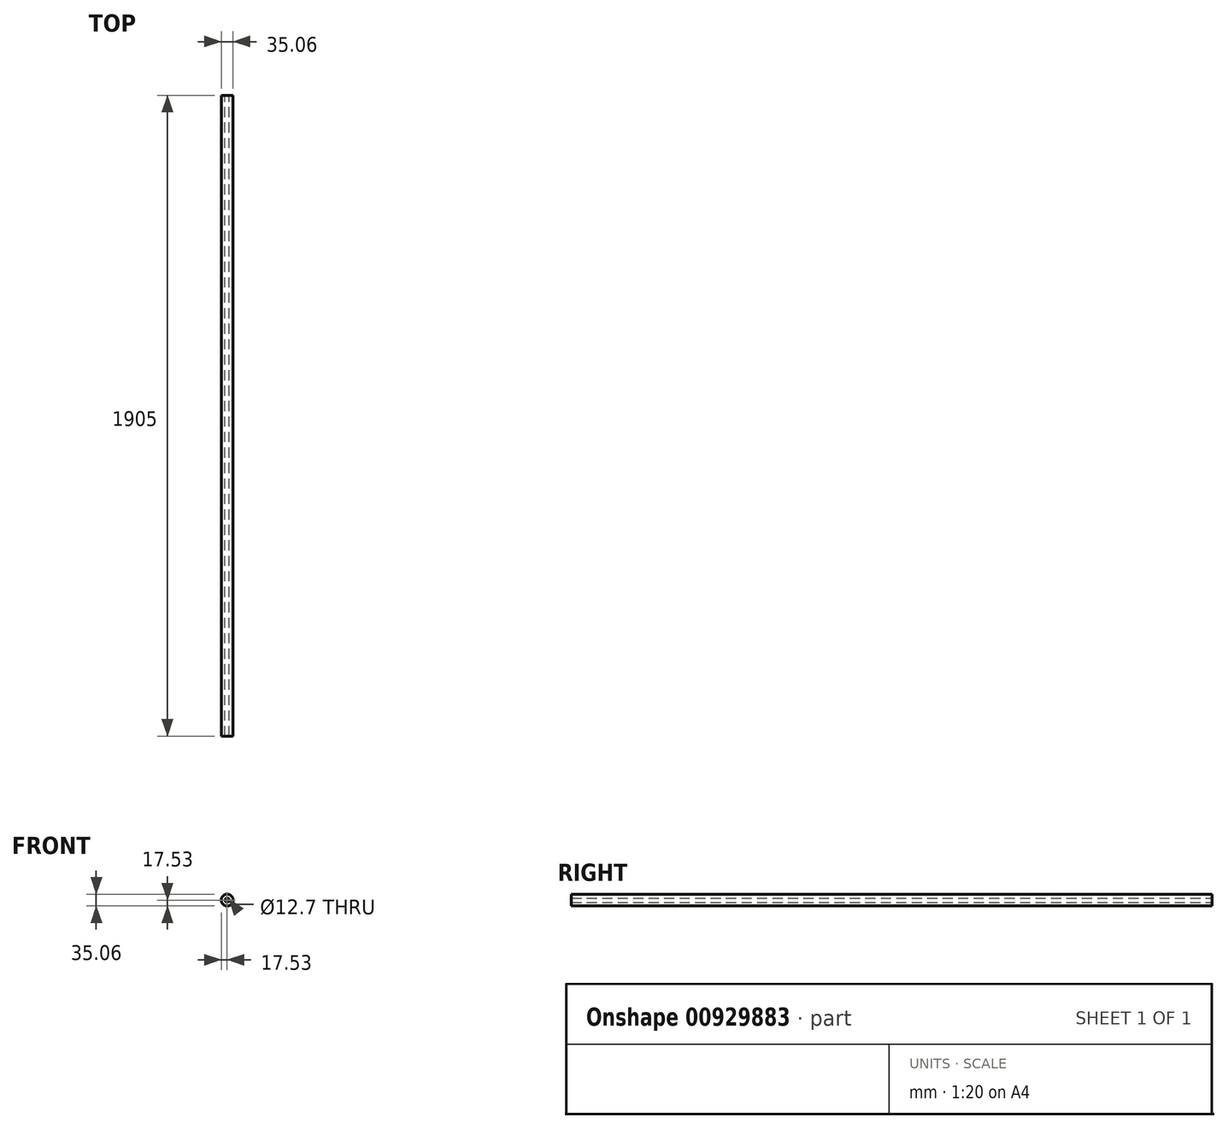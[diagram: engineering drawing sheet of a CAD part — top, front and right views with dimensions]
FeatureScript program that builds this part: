
annotation { "Feature Type Name" : "Feature", "Feature Type Description" : "" }
export const myFeature = defineFeature(function(context is Context, id is Id, definition is map)
    precondition{}
    {
        {
            assignVariable(context, id + "F0", {"name" : "StrutLength", "anyValue" : 1905 * mm});
        }
        {
            var Q0;
            Q0=qCreatedBy(makeId("Front.planeOp"),FACE);
            var sketch = newSketch(context, id + "F1", { "sketchPlane" : qUnion([Q0])});
            skCircle(sketch, "E0", {"center": v(0, 0) * mm, "radius": 6.35 * mm});
            skCircle(sketch, "E1", {"center": v(0, 0) * mm, "radius": 17.53 * mm});
            skSolve(sketch);
        }
        {
            var Q0;
            Q0=makeQuery(id+"F1.imprint","IMPRINT",FACE,{"disambiguationData":[TD([[makeQuery(id+"F1.imprint","IMPRINT",EDGE,{"derivedFrom":sQuery(id+"F1.wireOp",EDGE,"E0")}),-1.0]])]});
            extrude(context, id + "F2", {"entities" : qUnion([Q0]), "depth" : getVariable(context, 'StrutLength'), "offsetDistance" : 25.4 * mm});
        }
    });
